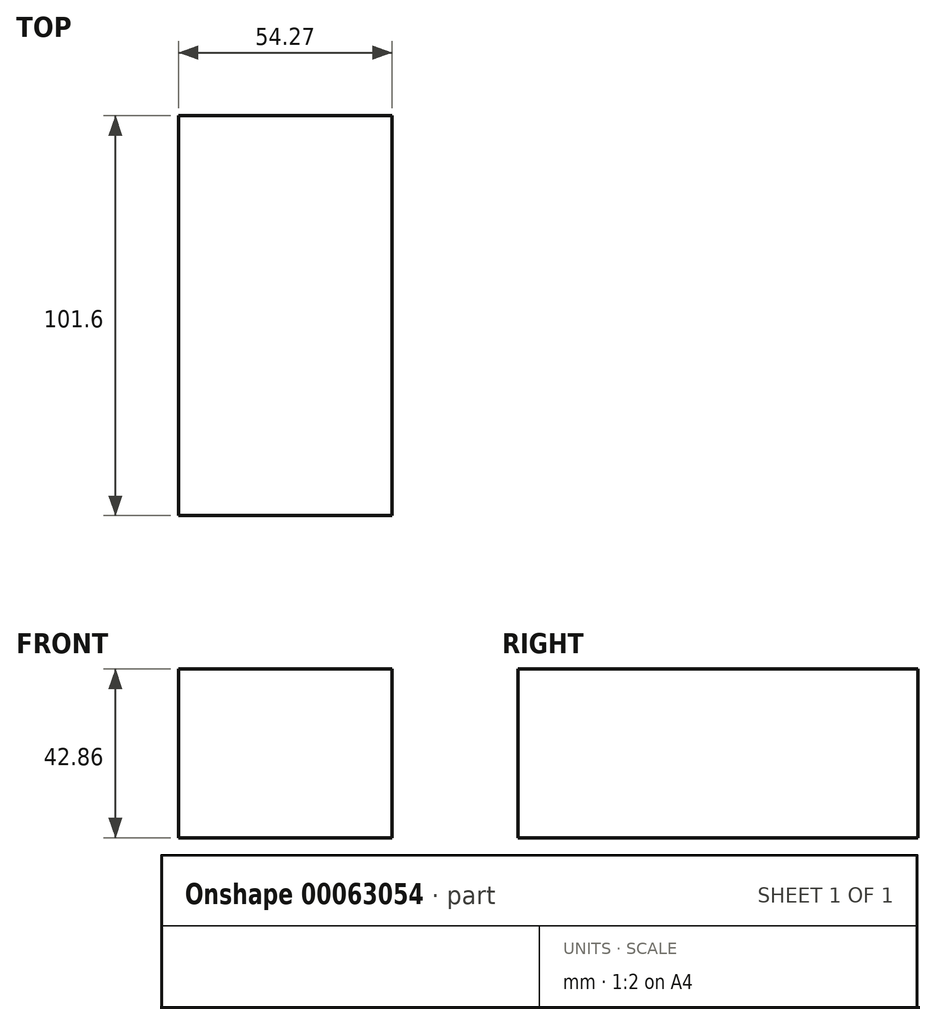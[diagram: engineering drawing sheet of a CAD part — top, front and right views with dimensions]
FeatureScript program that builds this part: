
annotation { "Feature Type Name" : "Feature", "Feature Type Description" : "" }
export const myFeature = defineFeature(function(context is Context, id is Id, definition is map)
    precondition{}
    {
        {
            var Q0;
            Q0=qCreatedBy(makeId("Front.planeOp"),FACE);
            var sketch = newSketch(context, id + "F0", { "sketchPlane" : qUnion([Q0])});
            skLineSegment(sketch, "E0.bottom", {"start": v(-14.19, 17.72) * mm, "end": v(40.08, 17.72) * mm});
            skLineSegment(sketch, "E0.top", {"start": v(-14.19, -25.14) * mm, "end": v(40.08, -25.14) * mm});
            skLineSegment(sketch, "E0.left", {"start": v(-14.19, 17.72) * mm, "end": v(-14.19, -25.14) * mm});
            skLineSegment(sketch, "E0.right", {"start": v(40.08, 17.72) * mm, "end": v(40.08, -25.14) * mm});
            skSolve(sketch);
        }
        {
            var Q0;
            Q0=makeQuery(id+"F0.imprint","IMPRINT",FACE,{"disambiguationData":[TD([[makeQuery(id+"F0.imprint","IMPRINT",EDGE,{"derivedFrom":sQuery(id+"F0.wireOp",EDGE,"E0.bottom")}),-1.0]])]});
            extrude(context, id + "F1", {"entities" : qUnion([Q0]), "depth" : 101.6 * mm});
        }
    });
